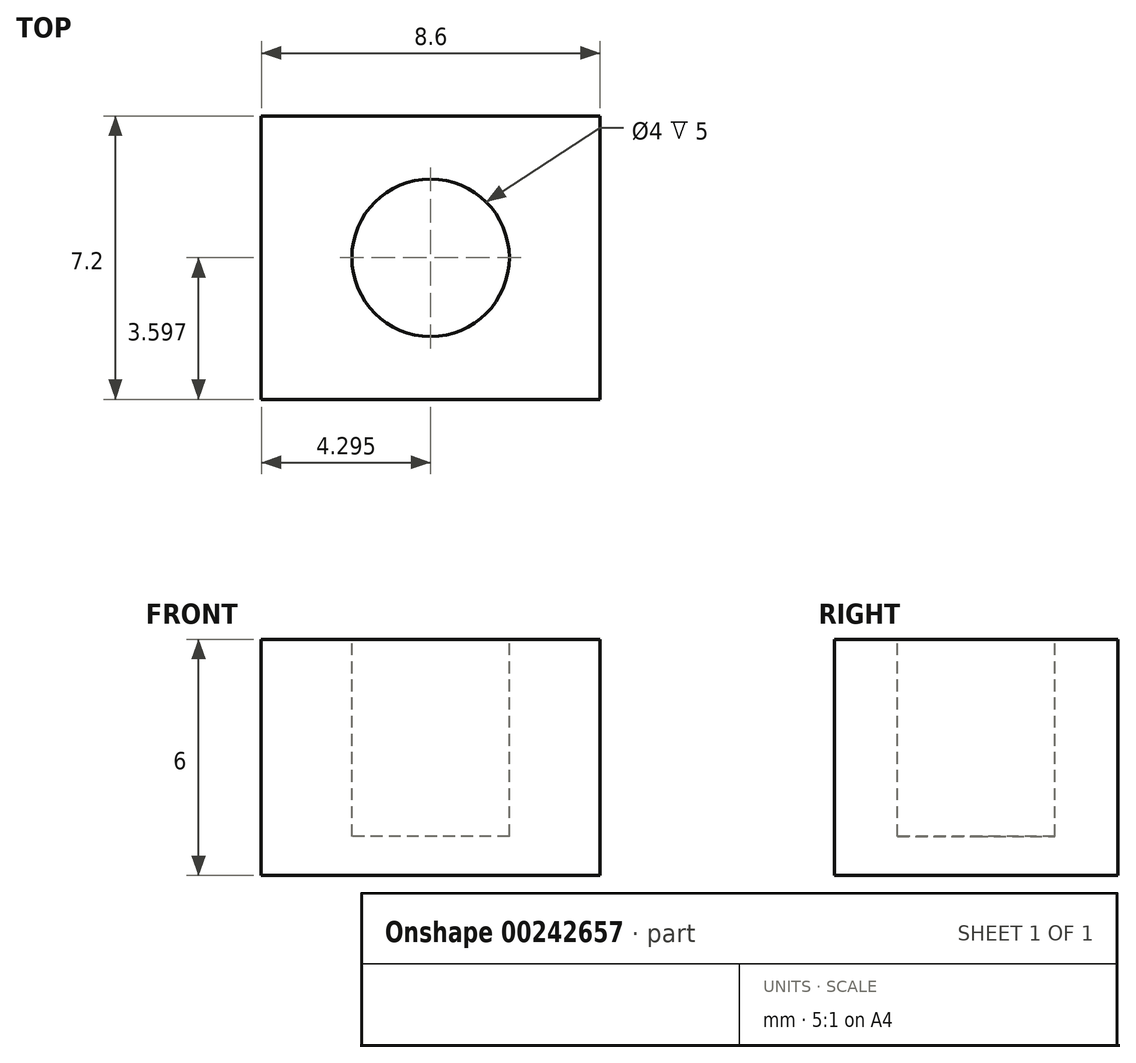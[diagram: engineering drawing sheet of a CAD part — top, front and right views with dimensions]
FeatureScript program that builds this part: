
annotation { "Feature Type Name" : "Feature", "Feature Type Description" : "" }
export const myFeature = defineFeature(function(context is Context, id is Id, definition is map)
    precondition{}
    {
        {
            var Q0;
            Q0=qCreatedBy(makeId("Top.planeOp"),FACE);
            var sketch = newSketch(context, id + "F0", { "sketchPlane" : qUnion([Q0])});
            skLineSegment(sketch, "E0.bottom", {"start": v(-66.06, 5.45) * mm, "end": v(-74.66, 5.45) * mm});
            skLineSegment(sketch, "E0.top", {"start": v(-66.06, 12.65) * mm, "end": v(-74.66, 12.65) * mm});
            skLineSegment(sketch, "E0.left", {"start": v(-66.06, 5.45) * mm, "end": v(-66.06, 12.65) * mm});
            skLineSegment(sketch, "E0.right", {"start": v(-74.66, 5.45) * mm, "end": v(-74.66, 12.65) * mm});
            skPoint(sketch, "E0.middle", {"position": v(-70.36, 9.05) * mm});
            skSolve(sketch);
        }
        {
            var Q0;
            Q0 = qSketchRegion(id + "F0", true);
            extrude(context, id + "F1", {"entities" : qUnion([Q0]), "depth" : 6 * mm});
        }
        {
            var Q0;
            Q0=makeQuery(id+"F1.opExtrude","CAP_FACE",FACE,{"disambiguationData":[OSD([sQuery(id+"F0.wireOp",EDGE,"E0.bottom"),sQuery(id+"F0.wireOp",EDGE,"E0.top"),sQuery(id+"F0.wireOp",EDGE,"E0.left"),sQuery(id+"F0.wireOp",EDGE,"E0.right")])],"isStart":false});
            var sketch = newSketch(context, id + "F2", { "sketchPlane" : qUnion([Q0])});
            skCircle(sketch, "E1", {"center": v(-70.36, 9.05) * mm, "radius": 2 * mm});
            skPoint(sketch, "E1.centerSnap0", {"position": v(-74.66, 9.05) * mm});
            skPoint(sketch, "E1.centerSnap1", {"position": v(-70.36, 12.65) * mm});
            skSolve(sketch);
        }
        {
            var Q0;
            Q0 = qSketchRegion(id + "F2", true);
            extrude(context, id + "F3", {"entities" : qUnion([Q0]), "operationType" : NewBodyOperationType.REMOVE, "oppositeDirection" : true, "depth" : 5 * mm});
        }
    });
